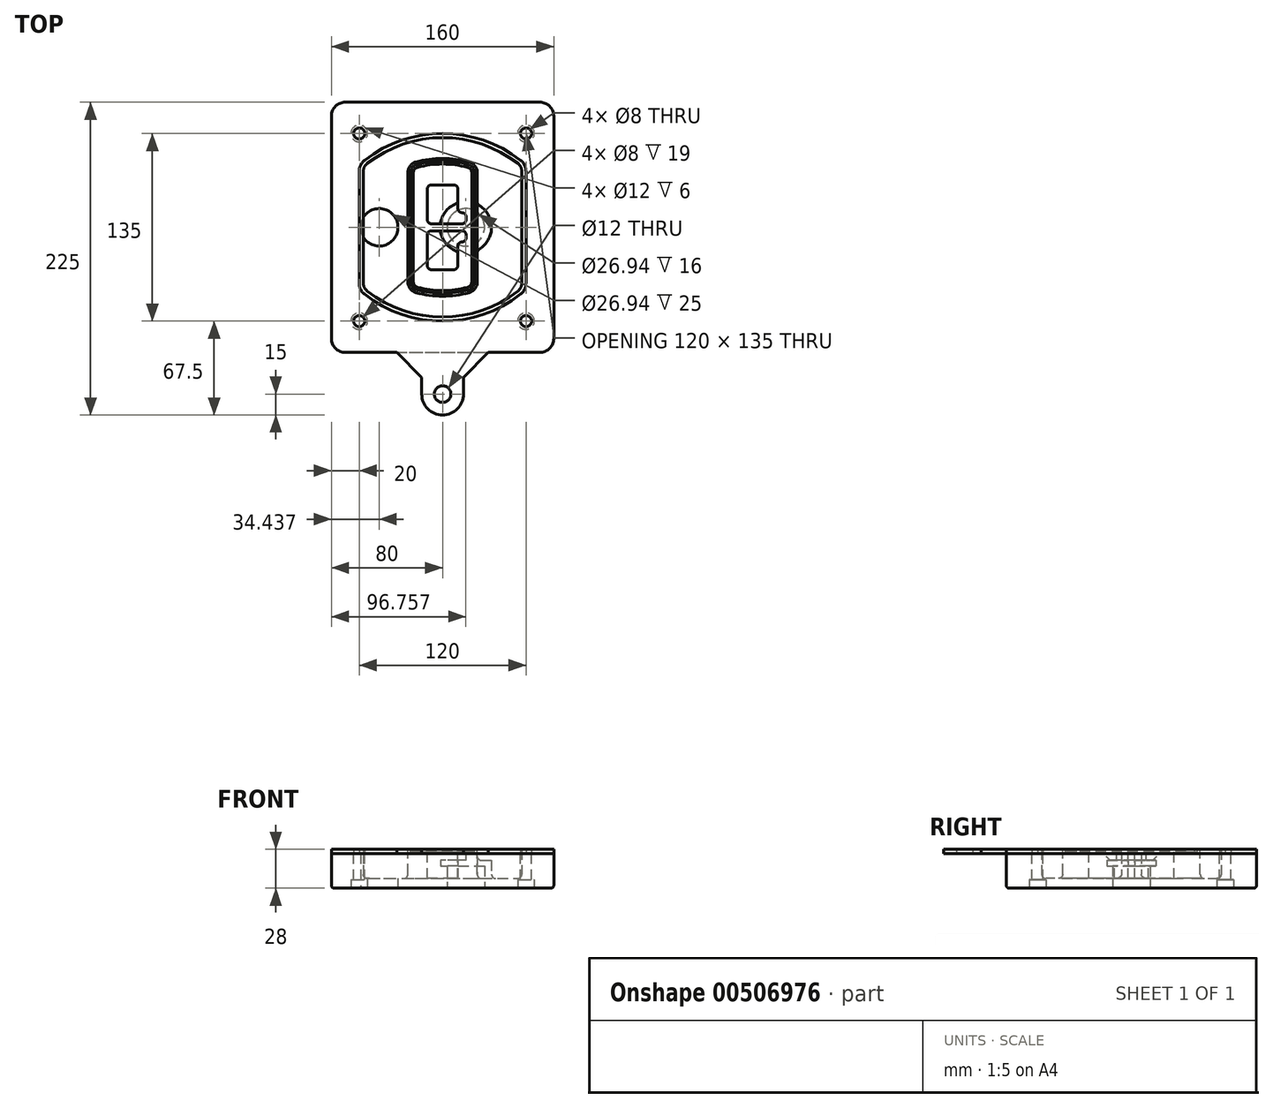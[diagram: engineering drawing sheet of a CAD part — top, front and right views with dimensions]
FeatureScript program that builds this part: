
annotation { "Feature Type Name" : "Feature", "Feature Type Description" : "" }
export const myFeature = defineFeature(function(context is Context, id is Id, definition is map)
    precondition{}
    {
        {
            var Q0;
            Q0=qCreatedBy(makeId("Top.planeOp"),FACE);
            var sketch = newSketch(context, id + "F0", { "sketchPlane" : qUnion([Q0])});
            skPoint(sketch, "E0.rect.middle", {"position": v(0, 0) * mm});
            skLineSegment(sketch, "E1.bottom", {"start": v(-70, -90) * mm, "end": v(70, -90) * mm});
            skLineSegment(sketch, "E1.top", {"start": v(-70, 90) * mm, "end": v(70, 90) * mm});
            skLineSegment(sketch, "E1.left", {"start": v(-80, -80) * mm, "end": v(-80, 80) * mm});
            skLineSegment(sketch, "E1.right", {"start": v(80, -80) * mm, "end": v(80, 80) * mm});
            skLineSegment(sketch, "E2", {"start": v(-80, 90) * mm, "end": v(80, -90) * mm, "construction": true});
            skLineSegment(sketch, "E3", {"start": v(80, 90) * mm, "end": v(-80, -90) * mm, "construction": true});
            skCircle(sketch, "E4", {"center": v(-60, 67.5) * mm, "radius": 4 * mm});
            skCircle(sketch, "E5", {"center": v(60, 67.5) * mm, "radius": 4 * mm});
            skCircle(sketch, "E6", {"center": v(60, -67.5) * mm, "radius": 4 * mm});
            skCircle(sketch, "E7", {"center": v(-60, -67.5) * mm, "radius": 4 * mm});
            skLineSegment(sketch, "E8", {"start": v(-60, 67.5) * mm, "end": v(60, 67.5) * mm, "construction": true});
            skLineSegment(sketch, "E9", {"start": v(60, 67.5) * mm, "end": v(60, -67.5) * mm, "construction": true});
            skLineSegment(sketch, "E10", {"start": v(60, -67.5) * mm, "end": v(-60, -67.5) * mm, "construction": true});
            skLineSegment(sketch, "E11", {"start": v(-60, -67.5) * mm, "end": v(-60, 67.5) * mm, "construction": true});
            skLineSegment(sketch, "E12", {"start": v(-60, 40.3) * mm, "end": v(-60, -40.3) * mm});
            skLineSegment(sketch, "E13", {"start": v(60, 40.3) * mm, "end": v(60, -40.3) * mm});
            skArc(sketch, "E14", {"start": v(56.15, 48.18) * mm, "mid": v(0, 67.5) * mm, "end": v(-56.15, 48.18) * mm});
            skArc(sketch, "E15", {"start": v(-56.15, -48.18) * mm, "mid": v(0, -67.5) * mm, "end": v(56.15, -48.18) * mm});
            skLineSegment(sketch, "E16", {"start": v(-60, 0) * mm, "end": v(60, 0) * mm, "construction": true});
            skPoint(sketch, "E17.visualSharp", {"position": v(-60, -45) * mm});
            skArc(sketch, "E17.filletArc", {"start": v(-60, -40.3) * mm, "mid": v(-58.99, -44.68) * mm, "end": v(-56.15, -48.18) * mm});
            skPoint(sketch, "E18.visualSharp", {"position": v(-60, 45) * mm});
            skArc(sketch, "E18.filletArc", {"start": v(-56.15, 48.18) * mm, "mid": v(-58.99, 44.68) * mm, "end": v(-60, 40.3) * mm});
            skPoint(sketch, "E19.visualSharp", {"position": v(60, 45) * mm});
            skArc(sketch, "E19.filletArc", {"start": v(60, 40.3) * mm, "mid": v(58.99, 44.68) * mm, "end": v(56.15, 48.18) * mm});
            skPoint(sketch, "E20.visualSharp", {"position": v(60, -45) * mm});
            skArc(sketch, "E20.filletArc", {"start": v(56.15, -48.18) * mm, "mid": v(58.99, -44.68) * mm, "end": v(60, -40.3) * mm});
            skPoint(sketch, "E21.visualSharp", {"position": v(-80, 90) * mm});
            skArc(sketch, "E21.filletArc", {"start": v(-70, 90) * mm, "mid": v(-77.07, 87.07) * mm, "end": v(-80, 80) * mm});
            skPoint(sketch, "E22.visualSharp", {"position": v(80, 90) * mm});
            skArc(sketch, "E22.filletArc", {"start": v(80, 80) * mm, "mid": v(77.07, 87.07) * mm, "end": v(70, 90) * mm});
            skPoint(sketch, "E23.visualSharp", {"position": v(80, -90) * mm});
            skArc(sketch, "E23.filletArc", {"start": v(70, -90) * mm, "mid": v(77.07, -87.07) * mm, "end": v(80, -80) * mm});
            skPoint(sketch, "E24.visualSharp", {"position": v(-80, -90) * mm});
            skArc(sketch, "E24.filletArc", {"start": v(-80, -80) * mm, "mid": v(-77.07, -87.07) * mm, "end": v(-70, -90) * mm});
            skArc(sketch, "E25.0", {"start": v(57, 40.3) * mm, "mid": v(56.3, 43.36) * mm, "end": v(54.3, 45.81) * mm});
            skLineSegment(sketch, "E25.1", {"start": v(57, 40.3) * mm, "end": v(57, -40.3) * mm});
            skArc(sketch, "E25.2", {"start": v(54.3, -45.81) * mm, "mid": v(56.3, -43.36) * mm, "end": v(57, -40.3) * mm});
            skArc(sketch, "E25.3", {"start": v(-54.3, -45.81) * mm, "mid": v(0, -64.5) * mm, "end": v(54.3, -45.81) * mm});
            skArc(sketch, "E25.4", {"start": v(-57, -40.3) * mm, "mid": v(-56.3, -43.36) * mm, "end": v(-54.3, -45.81) * mm});
            skArc(sketch, "E25.5", {"start": v(54.3, 45.81) * mm, "mid": v(0, 64.5) * mm, "end": v(-54.3, 45.81) * mm});
            skLineSegment(sketch, "E25.6", {"start": v(-57, 40.3) * mm, "end": v(-57, -40.3) * mm});
            skArc(sketch, "E25.7", {"start": v(-54.3, 45.81) * mm, "mid": v(-56.3, 43.36) * mm, "end": v(-57, 40.3) * mm});
            skArc(sketch, "E26.0", {"start": v(-58.62, 51.33) * mm, "mid": v(-62.58, 46.43) * mm, "end": v(-64, 40.3) * mm});
            skArc(sketch, "E26.1", {"start": v(58.62, 51.33) * mm, "mid": v(0, 71.5) * mm, "end": v(-58.62, 51.33) * mm});
            skArc(sketch, "E26.2", {"start": v(64, 40.3) * mm, "mid": v(62.58, 46.43) * mm, "end": v(58.62, 51.33) * mm});
            skLineSegment(sketch, "E26.3", {"start": v(64, 40.3) * mm, "end": v(64, -40.3) * mm});
            skArc(sketch, "E26.4", {"start": v(58.62, -51.33) * mm, "mid": v(62.58, -46.43) * mm, "end": v(64, -40.3) * mm});
            skLineSegment(sketch, "E26.5", {"start": v(-64, 40.3) * mm, "end": v(-64, -40.3) * mm});
            skArc(sketch, "E26.6", {"start": v(-58.62, -51.33) * mm, "mid": v(0, -71.5) * mm, "end": v(58.62, -51.33) * mm});
            skArc(sketch, "E26.7", {"start": v(-64, -40.3) * mm, "mid": v(-62.58, -46.43) * mm, "end": v(-58.62, -51.33) * mm});
            skSolve(sketch);
        }
        {
            var Q0;
            Q0=makeQuery(id+"F0.imprint","IMPRINT",FACE,{"disambiguationData":[TD([[makeQuery(id+"F0.imprint","IMPRINT",EDGE,{"derivedFrom":sQuery(id+"F0.wireOp",EDGE,"E1.bottom")}),1.0]])]});
            var Q1;
            Q1=makeQuery(id+"F0.imprint","IMPRINT",FACE,{"disambiguationData":[TD([[makeQuery(id+"F0.imprint","IMPRINT",EDGE,{"derivedFrom":sQuery(id+"F0.wireOp",EDGE,"E12")}),1.0]])]});
            var Q2;
            Q2=makeQuery(id+"F0.imprint","IMPRINT",FACE,{"disambiguationData":[TD([[makeQuery(id+"F0.imprint","IMPRINT",EDGE,{"derivedFrom":sQuery(id+"F0.wireOp",EDGE,"E25.0")}),1.0]])]});
            var Q3;
            Q3=makeQuery(id+"F0.imprint","IMPRINT",FACE,{"disambiguationData":[TD([[makeQuery(id+"F0.imprint","IMPRINT",EDGE,{"derivedFrom":sQuery(id+"F0.wireOp",EDGE,"E12")}),-1.0]])]});
            extrude(context, id + "F1", {"entities" : qUnion([Q0, Q1, Q2, Q3]), "oppositeDirection" : true, "depth" : 25 * mm});
        }
        {
            var Q0;
            Q0=makeQuery(id+"F0.imprint","IMPRINT",FACE,{"disambiguationData":[TD([[makeQuery(id+"F0.imprint","IMPRINT",EDGE,{"derivedFrom":sQuery(id+"F0.wireOp",EDGE,"E12")}),1.0]])]});
            extrude(context, id + "F2", {"entities" : qUnion([Q0]), "operationType" : NewBodyOperationType.ADD, "depth" : 3 * mm});
        }
        {
            var Q0;
            Q0=makeQuery(id+"F0.imprint","IMPRINT",FACE,{"disambiguationData":[TD([[makeQuery(id+"F0.imprint","IMPRINT",EDGE,{"derivedFrom":sQuery(id+"F0.wireOp",EDGE,"E25.0")}),1.0]])]});
            extrude(context, id + "F3", {"entities" : qUnion([Q0]), "operationType" : NewBodyOperationType.REMOVE, "oppositeDirection" : true, "depth" : 18 * mm});
        }
        {
            var Q0;
            Q0=makeQuery(id+"F2.opExtrude","CAP_FACE",FACE,{"disambiguationData":[OSD([sQuery(id+"F0.wireOp",EDGE,"E12"),sQuery(id+"F0.wireOp",EDGE,"E13"),sQuery(id+"F0.wireOp",EDGE,"E14"),sQuery(id+"F0.wireOp",EDGE,"E15"),sQuery(id+"F0.wireOp",EDGE,"E17.filletArc"),sQuery(id+"F0.wireOp",EDGE,"E18.filletArc"),sQuery(id+"F0.wireOp",EDGE,"E19.filletArc"),sQuery(id+"F0.wireOp",EDGE,"E20.filletArc"),sQuery(id+"F0.wireOp",EDGE,"E25.0"),sQuery(id+"F0.wireOp",EDGE,"E25.1"),sQuery(id+"F0.wireOp",EDGE,"E25.2"),sQuery(id+"F0.wireOp",EDGE,"E25.3"),sQuery(id+"F0.wireOp",EDGE,"E25.4"),sQuery(id+"F0.wireOp",EDGE,"E25.5"),sQuery(id+"F0.wireOp",EDGE,"E25.6"),sQuery(id+"F0.wireOp",EDGE,"E25.7")])],"isStart":false});
            var sketch = newSketch(context, id + "F4", { "sketchPlane" : qUnion([Q0])});
            skArc(sketch, "E27.0", {"start": v(-19.08, -46.97) * mm, "mid": v(0, -49.5) * mm, "end": v(19.08, -46.97) * mm});
            skArc(sketch, "E28.0", {"start": v(19.08, 46.97) * mm, "mid": v(0, 49.5) * mm, "end": v(-19.08, 46.97) * mm});
            skLineSegment(sketch, "E29", {"start": v(-25, 39.25) * mm, "end": v(-25, -39.25) * mm});
            skLineSegment(sketch, "E30", {"start": v(25, 39.25) * mm, "end": v(25, -39.25) * mm});
            skLineSegment(sketch, "E31", {"start": v(-25, 45.1) * mm, "end": v(25, 45.1) * mm, "construction": true});
            skLineSegment(sketch, "E32", {"start": v(-25, -45.1) * mm, "end": v(25, -45.1) * mm, "construction": true});
            skPoint(sketch, "E33.visualSharp", {"position": v(-25, 45.1) * mm});
            skArc(sketch, "E33.filletArc", {"start": v(-19.08, 46.97) * mm, "mid": v(-23.35, 44.11) * mm, "end": v(-25, 39.25) * mm});
            skPoint(sketch, "E34.visualSharp", {"position": v(25, 45.1) * mm});
            skArc(sketch, "E34.filletArc", {"start": v(25, 39.25) * mm, "mid": v(23.35, 44.11) * mm, "end": v(19.08, 46.97) * mm});
            skPoint(sketch, "E35.visualSharp", {"position": v(25, -45.1) * mm});
            skArc(sketch, "E35.filletArc", {"start": v(19.08, -46.97) * mm, "mid": v(23.35, -44.11) * mm, "end": v(25, -39.25) * mm});
            skPoint(sketch, "E36.visualSharp", {"position": v(-25, -45.1) * mm});
            skArc(sketch, "E36.filletArc", {"start": v(-25, -39.25) * mm, "mid": v(-23.35, -44.11) * mm, "end": v(-19.08, -46.97) * mm});
            skArc(sketch, "E37.0", {"start": v(54.3, 45.81) * mm, "mid": v(0, 64.5) * mm, "end": v(-54.3, 45.81) * mm});
            skArc(sketch, "E37.1", {"start": v(-54.3, 45.81) * mm, "mid": v(-56.3, 43.36) * mm, "end": v(-57, 40.3) * mm});
            skLineSegment(sketch, "E37.2", {"start": v(-57, 40.3) * mm, "end": v(-57, -40.3) * mm});
            skArc(sketch, "E37.3", {"start": v(-57, -40.3) * mm, "mid": v(-56.3, -43.36) * mm, "end": v(-54.3, -45.81) * mm});
            skArc(sketch, "E37.4", {"start": v(-54.3, -45.81) * mm, "mid": v(0, -64.5) * mm, "end": v(54.3, -45.81) * mm});
            skArc(sketch, "E37.5", {"start": v(54.3, -45.81) * mm, "mid": v(56.3, -43.36) * mm, "end": v(57, -40.3) * mm});
            skLineSegment(sketch, "E37.6", {"start": v(57, 40.3) * mm, "end": v(57, -40.3) * mm});
            skArc(sketch, "E37.7", {"start": v(57, 40.3) * mm, "mid": v(56.3, 43.36) * mm, "end": v(54.3, 45.81) * mm});
            skLineSegment(sketch, "E38.0", {"start": v(23, 39.25) * mm, "end": v(23, -39.25) * mm});
            skArc(sketch, "E38.1", {"start": v(18.56, -45.04) * mm, "mid": v(21.76, -42.9) * mm, "end": v(23, -39.25) * mm});
            skArc(sketch, "E38.2", {"start": v(-18.56, -45.04) * mm, "mid": v(0, -47.5) * mm, "end": v(18.56, -45.04) * mm});
            skArc(sketch, "E38.3", {"start": v(-23, -39.25) * mm, "mid": v(-21.76, -42.9) * mm, "end": v(-18.56, -45.04) * mm});
            skLineSegment(sketch, "E38.4", {"start": v(-23, 39.25) * mm, "end": v(-23, -39.25) * mm});
            skArc(sketch, "E38.5", {"start": v(23, 39.25) * mm, "mid": v(21.76, 42.9) * mm, "end": v(18.56, 45.04) * mm});
            skArc(sketch, "E38.6", {"start": v(-18.56, 45.04) * mm, "mid": v(-21.76, 42.9) * mm, "end": v(-23, 39.25) * mm});
            skArc(sketch, "E38.7", {"start": v(18.56, 45.04) * mm, "mid": v(0, 47.5) * mm, "end": v(-18.56, 45.04) * mm});
            skArc(sketch, "E39.0", {"start": v(21, 39.25) * mm, "mid": v(20.18, 41.68) * mm, "end": v(18.04, 43.1) * mm});
            skLineSegment(sketch, "E39.1", {"start": v(21, 39.25) * mm, "end": v(21, -39.25) * mm});
            skArc(sketch, "E39.2", {"start": v(18.04, -43.1) * mm, "mid": v(20.18, -41.68) * mm, "end": v(21, -39.25) * mm});
            skArc(sketch, "E39.3", {"start": v(-18.04, -43.1) * mm, "mid": v(0, -45.5) * mm, "end": v(18.04, -43.1) * mm});
            skArc(sketch, "E39.4", {"start": v(-21, -39.25) * mm, "mid": v(-20.18, -41.68) * mm, "end": v(-18.04, -43.1) * mm});
            skArc(sketch, "E39.5", {"start": v(18.04, 43.1) * mm, "mid": v(0, 45.5) * mm, "end": v(-18.04, 43.1) * mm});
            skLineSegment(sketch, "E39.6", {"start": v(-21, 39.25) * mm, "end": v(-21, -39.25) * mm});
            skArc(sketch, "E39.7", {"start": v(-18.04, 43.1) * mm, "mid": v(-20.18, 41.68) * mm, "end": v(-21, 39.25) * mm});
            skLineSegment(sketch, "E40", {"start": v(-25, 0) * mm, "end": v(25, 0) * mm, "construction": true});
            skLineSegment(sketch, "E41", {"start": v(-11, 5.5) * mm, "end": v(-11, 27.5) * mm});
            skLineSegment(sketch, "E42", {"start": v(-8, 30.5) * mm, "end": v(8, 30.5) * mm});
            skLineSegment(sketch, "E43", {"start": v(11, 27.5) * mm, "end": v(11, 13.5) * mm});
            skLineSegment(sketch, "E44", {"start": v(14, 10.5) * mm, "end": v(14, 10.5) * mm});
            skLineSegment(sketch, "E45", {"start": v(17, 7.5) * mm, "end": v(17, 5.5) * mm});
            skLineSegment(sketch, "E46", {"start": v(14, 2.5) * mm, "end": v(-8, 2.5) * mm});
            skPoint(sketch, "E47.visualSharp", {"position": v(-11, 30.5) * mm});
            skArc(sketch, "E47.filletArc", {"start": v(-8, 30.5) * mm, "mid": v(-10.12, 29.62) * mm, "end": v(-11, 27.5) * mm});
            skPoint(sketch, "E48.visualSharp", {"position": v(11, 30.5) * mm});
            skArc(sketch, "E48.filletArc", {"start": v(11, 27.5) * mm, "mid": v(10.12, 29.62) * mm, "end": v(8, 30.5) * mm});
            skPoint(sketch, "E49.visualSharp", {"position": v(11, 10.5) * mm});
            skArc(sketch, "E49.filletArc", {"start": v(11, 13.5) * mm, "mid": v(11.88, 11.38) * mm, "end": v(14, 10.5) * mm});
            skPoint(sketch, "E50.visualSharp", {"position": v(17, 10.5) * mm});
            skArc(sketch, "E50.filletArc", {"start": v(17, 7.5) * mm, "mid": v(16.12, 9.62) * mm, "end": v(14, 10.5) * mm});
            skPoint(sketch, "E51.visualSharp", {"position": v(17, 2.5) * mm});
            skArc(sketch, "E51.filletArc", {"start": v(14, 2.5) * mm, "mid": v(16.12, 3.38) * mm, "end": v(17, 5.5) * mm});
            skPoint(sketch, "E52.visualSharp", {"position": v(-11, 2.5) * mm});
            skArc(sketch, "E52.filletArc", {"start": v(-11, 5.5) * mm, "mid": v(-10.12, 3.38) * mm, "end": v(-8, 2.5) * mm});
            skLineSegment(sketch, "E53.0.MirrorCS", {"start": v(14, -2.5) * mm, "end": v(-8, -2.5) * mm});
            skArc(sketch, "E54.0.MirrorCS", {"start": v(-11, -5.5) * mm, "mid": v(-10.12, -3.38) * mm, "end": v(-8, -2.5) * mm});
            skLineSegment(sketch, "E55.0.MirrorCS", {"start": v(-11, -5.5) * mm, "end": v(-11, -27.5) * mm});
            skArc(sketch, "E56.0.MirrorCS", {"start": v(-8, -30.5) * mm, "mid": v(-10.12, -29.62) * mm, "end": v(-11, -27.5) * mm});
            skLineSegment(sketch, "E57.0.MirrorCS", {"start": v(-8, -30.5) * mm, "end": v(8, -30.5) * mm});
            skArc(sketch, "E58.0.MirrorCS", {"start": v(11, -27.5) * mm, "mid": v(10.12, -29.62) * mm, "end": v(8, -30.5) * mm});
            skLineSegment(sketch, "E59.0.MirrorCS", {"start": v(11, -27.5) * mm, "end": v(11, -13.5) * mm});
            skArc(sketch, "E60.0.MirrorCS", {"start": v(11, -13.5) * mm, "mid": v(11.88, -11.38) * mm, "end": v(14, -10.5) * mm});
            skArc(sketch, "E61.0.MirrorCS", {"start": v(17, -7.5) * mm, "mid": v(16.12, -9.62) * mm, "end": v(14, -10.5) * mm});
            skLineSegment(sketch, "E62.0.MirrorCS", {"start": v(17, -7.5) * mm, "end": v(17, -5.5) * mm});
            skArc(sketch, "E63.0.MirrorCS", {"start": v(14, -2.5) * mm, "mid": v(16.12, -3.38) * mm, "end": v(17, -5.5) * mm});
            skSolve(sketch);
        }
        {
            var Q0;
            Q0=makeQuery(id+"F4.imprint","IMPRINT",FACE,{"disambiguationData":[TD([[makeQuery(id+"F4.imprint","IMPRINT",EDGE,{"derivedFrom":sQuery(id+"F4.wireOp",EDGE,"E27.0")}),1.0]])]});
            var Q1;
            Q1=makeQuery(id+"F4.imprint","IMPRINT",FACE,{"disambiguationData":[TD([[makeQuery(id+"F4.imprint","IMPRINT",EDGE,{"derivedFrom":sQuery(id+"F4.wireOp",EDGE,"E38.0")}),-1.0]])]});
            var Q2;
            Q2=makeQuery(id+"F4.imprint","IMPRINT",FACE,{"disambiguationData":[TD([[makeQuery(id+"F4.imprint","IMPRINT",EDGE,{"derivedFrom":sQuery(id+"F4.wireOp",EDGE,"E39.0")}),1.0]])]});
            extrude(context, id + "F5", {"entities" : qUnion([Q0, Q1, Q2]), "operationType" : NewBodyOperationType.ADD, "endBound" : BoundingType.UP_TO_NEXT, "oppositeDirection" : true, "depth" : 25 * mm});
        }
        {
            var Q0;
            Q0=makeQuery(id+"F4.imprint","IMPRINT",FACE,{"disambiguationData":[TD([[makeQuery(id+"F4.imprint","IMPRINT",EDGE,{"derivedFrom":sQuery(id+"F4.wireOp",EDGE,"E38.0")}),-1.0]])]});
            extrude(context, id + "F6", {"entities" : qUnion([Q0]), "operationType" : NewBodyOperationType.REMOVE, "oppositeDirection" : true, "depth" : 2 * mm});
        }
        {
            var Q0;
            Q0=makeQuery(id+"F1.opExtrude","CAP_FACE",FACE,{"disambiguationData":[OSD([sQuery(id+"F0.wireOp",EDGE,"E1.bottom"),sQuery(id+"F0.wireOp",EDGE,"E1.top"),sQuery(id+"F0.wireOp",EDGE,"E1.left"),sQuery(id+"F0.wireOp",EDGE,"E1.right"),sQuery(id+"F0.wireOp",EDGE,"E4"),sQuery(id+"F0.wireOp",EDGE,"E5"),sQuery(id+"F0.wireOp",EDGE,"E6"),sQuery(id+"F0.wireOp",EDGE,"E7"),sQuery(id+"F0.wireOp",EDGE,"E21.filletArc"),sQuery(id+"F0.wireOp",EDGE,"E22.filletArc"),sQuery(id+"F0.wireOp",EDGE,"E23.filletArc"),sQuery(id+"F0.wireOp",EDGE,"E24.filletArc")])],"isStart":false});
            var sketch = newSketch(context, id + "F7", { "sketchPlane" : qUnion([Q0])});
            skCircle(sketch, "E64", {"center": v(16.76, 0) * mm, "radius": 13.47 * mm});
            skCircle(sketch, "E65", {"center": v(-45.56, 0) * mm, "radius": 13.47 * mm});
            skLineSegment(sketch, "E66", {"start": v(80, 0) * mm, "end": v(-80, 0) * mm});
            skCircle(sketch, "E67", {"center": v(16.76, 0) * mm, "radius": 18.47 * mm});
            skCircle(sketch, "E68", {"center": v(60, -67.5) * mm, "radius": 6 * mm});
            skCircle(sketch, "E69", {"center": v(-60, -67.5) * mm, "radius": 6 * mm});
            skCircle(sketch, "E70", {"center": v(-60, 67.5) * mm, "radius": 6 * mm});
            skCircle(sketch, "E71", {"center": v(60, 67.5) * mm, "radius": 6 * mm});
            skSolve(sketch);
        }
        {
            var Q0;
            {var subQ1=sQuery(id+"F7.wireOp",EDGE,"E66");var subQ4=sQuery(id+"F7.wireOp",EDGE,"E64");var subQ6=makeQuery(id+"F7.imprint","INTERSECT",VERTEX,{"disambiguationData":[OD(0.0)],"derivedFrom":[subQ4,subQ1]});Q0=makeQuery(id+"F7.imprint","IMPRINT",FACE,{"disambiguationData":[TD([[makeQuery(id+"F7.imprint","IMPRINT",EDGE,{"disambiguationData":[TD([[subQ6,-1.0]])],"derivedFrom":subQ4}),-1.0]])]});}
            var Q1;
            {var subQ0=sQuery(id+"F7.wireOp",EDGE,"E66");var subQ1=sQuery(id+"F7.wireOp",EDGE,"E64");var subQ3=makeQuery(id+"F7.imprint","INTERSECT",VERTEX,{"disambiguationData":[OD(0.0)],"derivedFrom":[subQ1,subQ0]});Q1=makeQuery(id+"F7.imprint","IMPRINT",FACE,{"disambiguationData":[TD([[makeQuery(id+"F7.imprint","IMPRINT",EDGE,{"disambiguationData":[TD([[subQ3,-1.0]])],"derivedFrom":subQ1}),1.0]])]});}
            var Q2;
            {var subQ0=sQuery(id+"F7.wireOp",EDGE,"E66");var subQ1=sQuery(id+"F7.wireOp",EDGE,"E64");var subQ3=makeQuery(id+"F7.imprint","INTERSECT",VERTEX,{"disambiguationData":[OD(0.0)],"derivedFrom":[subQ1,subQ0]});Q2=makeQuery(id+"F7.imprint","IMPRINT",FACE,{"disambiguationData":[TD([[makeQuery(id+"F7.imprint","IMPRINT",EDGE,{"disambiguationData":[TD([[subQ3,1.0]])],"derivedFrom":subQ1}),1.0]])]});}
            var Q3;
            {var subQ1=sQuery(id+"F7.wireOp",EDGE,"E66");var subQ4=sQuery(id+"F7.wireOp",EDGE,"E64");var subQ6=makeQuery(id+"F7.imprint","INTERSECT",VERTEX,{"disambiguationData":[OD(0.0)],"derivedFrom":[subQ4,subQ1]});Q3=makeQuery(id+"F7.imprint","IMPRINT",FACE,{"disambiguationData":[TD([[makeQuery(id+"F7.imprint","IMPRINT",EDGE,{"disambiguationData":[TD([[subQ6,1.0]])],"derivedFrom":subQ4}),-1.0]])]});}
            extrude(context, id + "F8", {"entities" : qUnion([Q0, Q1, Q2, Q3]), "operationType" : NewBodyOperationType.ADD, "oppositeDirection" : true, "depth" : 20 * mm});
        }
        {
            var Q0;
            {var subQ0=sQuery(id+"F7.wireOp",EDGE,"E66");var subQ1=sQuery(id+"F7.wireOp",EDGE,"E64");var subQ3=makeQuery(id+"F7.imprint","INTERSECT",VERTEX,{"disambiguationData":[OD(0.0)],"derivedFrom":[subQ1,subQ0]});Q0=makeQuery(id+"F7.imprint","IMPRINT",FACE,{"disambiguationData":[TD([[makeQuery(id+"F7.imprint","IMPRINT",EDGE,{"disambiguationData":[TD([[subQ3,-1.0]])],"derivedFrom":subQ1}),1.0]])]});}
            var Q1;
            {var subQ0=sQuery(id+"F7.wireOp",EDGE,"E66");var subQ1=sQuery(id+"F7.wireOp",EDGE,"E64");var subQ3=makeQuery(id+"F7.imprint","INTERSECT",VERTEX,{"disambiguationData":[OD(0.0)],"derivedFrom":[subQ1,subQ0]});Q1=makeQuery(id+"F7.imprint","IMPRINT",FACE,{"disambiguationData":[TD([[makeQuery(id+"F7.imprint","IMPRINT",EDGE,{"disambiguationData":[TD([[subQ3,1.0]])],"derivedFrom":subQ1}),1.0]])]});}
            extrude(context, id + "F9", {"entities" : qUnion([Q0, Q1]), "operationType" : NewBodyOperationType.REMOVE, "oppositeDirection" : true, "depth" : 16 * mm});
        }
        {
            var Q0;
            {var subQ0=sQuery(id+"F7.wireOp",EDGE,"E66");var subQ1=sQuery(id+"F7.wireOp",EDGE,"E65");var subQ3=makeQuery(id+"F7.imprint","INTERSECT",VERTEX,{"disambiguationData":[OD(0.0)],"derivedFrom":[subQ1,subQ0]});Q0=makeQuery(id+"F7.imprint","IMPRINT",FACE,{"disambiguationData":[TD([[makeQuery(id+"F7.imprint","IMPRINT",EDGE,{"disambiguationData":[TD([[subQ3,-1.0]])],"derivedFrom":subQ1}),1.0]])]});}
            var Q1;
            {var subQ0=sQuery(id+"F7.wireOp",EDGE,"E66");var subQ1=sQuery(id+"F7.wireOp",EDGE,"E65");var subQ3=makeQuery(id+"F7.imprint","INTERSECT",VERTEX,{"disambiguationData":[OD(0.0)],"derivedFrom":[subQ1,subQ0]});Q1=makeQuery(id+"F7.imprint","IMPRINT",FACE,{"disambiguationData":[TD([[makeQuery(id+"F7.imprint","IMPRINT",EDGE,{"disambiguationData":[TD([[subQ3,1.0]])],"derivedFrom":subQ1}),1.0]])]});}
            extrude(context, id + "F10", {"entities" : qUnion([Q0, Q1]), "operationType" : NewBodyOperationType.REMOVE, "oppositeDirection" : true, "depth" : 25 * mm});
        }
        {
            var Q0;
            Q0=makeQuery(id+"F7.imprint","IMPRINT",FACE,{"disambiguationData":[TD([[makeQuery(id+"F7.imprint","IMPRINT",EDGE,{"derivedFrom":sQuery(id+"F7.wireOp",EDGE,"E68")}),1.0]])]});
            var Q1;
            Q1=makeQuery(id+"F7.imprint","IMPRINT",FACE,{"disambiguationData":[TD([[makeQuery(id+"F7.imprint","IMPRINT",EDGE,{"derivedFrom":makeQuery(id+"F1.opExtrude","CAP_EDGE",EDGE,{"disambiguationData":[OSD([sQuery(id+"F0.wireOp",EDGE,"E5")])],"isStart":false})}),-1.0]])]});
            var Q2;
            Q2=makeQuery(id+"F7.imprint","IMPRINT",FACE,{"disambiguationData":[TD([[makeQuery(id+"F7.imprint","IMPRINT",EDGE,{"derivedFrom":sQuery(id+"F7.wireOp",EDGE,"E69")}),1.0]])]});
            var Q3;
            Q3=makeQuery(id+"F7.imprint","IMPRINT",FACE,{"disambiguationData":[TD([[makeQuery(id+"F7.imprint","IMPRINT",EDGE,{"derivedFrom":makeQuery(id+"F1.opExtrude","CAP_EDGE",EDGE,{"disambiguationData":[OSD([sQuery(id+"F0.wireOp",EDGE,"E4")])],"isStart":false})}),-1.0]])]});
            var Q4;
            Q4=makeQuery(id+"F7.imprint","IMPRINT",FACE,{"disambiguationData":[TD([[makeQuery(id+"F7.imprint","IMPRINT",EDGE,{"derivedFrom":sQuery(id+"F7.wireOp",EDGE,"E70")}),1.0]])]});
            var Q5;
            Q5=makeQuery(id+"F7.imprint","IMPRINT",FACE,{"disambiguationData":[TD([[makeQuery(id+"F7.imprint","IMPRINT",EDGE,{"derivedFrom":makeQuery(id+"F1.opExtrude","CAP_EDGE",EDGE,{"disambiguationData":[OSD([sQuery(id+"F0.wireOp",EDGE,"E7")])],"isStart":false})}),-1.0]])]});
            var Q6;
            Q6=makeQuery(id+"F7.imprint","IMPRINT",FACE,{"disambiguationData":[TD([[makeQuery(id+"F7.imprint","IMPRINT",EDGE,{"derivedFrom":sQuery(id+"F7.wireOp",EDGE,"E71")}),1.0]])]});
            var Q7;
            Q7=makeQuery(id+"F7.imprint","IMPRINT",FACE,{"disambiguationData":[TD([[makeQuery(id+"F7.imprint","IMPRINT",EDGE,{"derivedFrom":makeQuery(id+"F1.opExtrude","CAP_EDGE",EDGE,{"disambiguationData":[OSD([sQuery(id+"F0.wireOp",EDGE,"E6")])],"isStart":false})}),-1.0]])]});
            extrude(context, id + "F11", {"entities" : qUnion([Q0, Q1, Q2, Q3, Q4, Q5, Q6, Q7]), "operationType" : NewBodyOperationType.REMOVE, "oppositeDirection" : true, "depth" : 6 * mm});
        }
        {
            var Q0;
            Q0=makeQuery(id+"F9.boolean.opBoolean","COPY",FACE,{"derivedFrom":makeQuery(id+"F9.opExtrude","CAP_FACE",FACE,{"disambiguationData":[OSD([sQuery(id+"F7.wireOp",EDGE,"E64")])],"isStart":false})});
            var sketch = newSketch(context, id + "F12", { "sketchPlane" : qUnion([Q0])});
            skArc(sketch, "E72.0", {"start": v(11, 17.55) * mm, "mid": v(2.57, 11.82) * mm, "end": v(-1.54, 2.5) * mm});
            skArc(sketch, "E72.1", {"start": v(-1.54, -2.5) * mm, "mid": v(2.57, -11.82) * mm, "end": v(11, -17.55) * mm});
            skLineSegment(sketch, "E73", {"start": v(-1.54, -2.5) * mm, "end": v(14, -2.5) * mm});
            skLineSegment(sketch, "E74.0", {"start": v(14, 2.5) * mm, "end": v(-1.54, 2.5) * mm});
            skArc(sketch, "E74.1", {"start": v(14, 2.5) * mm, "mid": v(16.12, 3.38) * mm, "end": v(17, 5.5) * mm});
            skLineSegment(sketch, "E74.2", {"start": v(17, 7.5) * mm, "end": v(17, 5.5) * mm});
            skArc(sketch, "E74.3", {"start": v(17, 7.5) * mm, "mid": v(16.12, 9.62) * mm, "end": v(14, 10.5) * mm});
            skArc(sketch, "E74.4", {"start": v(11, 13.5) * mm, "mid": v(11.88, 11.38) * mm, "end": v(14, 10.5) * mm});
            skLineSegment(sketch, "E74.5", {"start": v(11, 17.55) * mm, "end": v(11, 13.5) * mm});
            skLineSegment(sketch, "E74.7", {"start": v(14, -2.5) * mm, "end": v(-1.54, -2.5) * mm});
            skArc(sketch, "E74.8", {"start": v(14, -2.5) * mm, "mid": v(16.12, -3.38) * mm, "end": v(17, -5.5) * mm});
            skLineSegment(sketch, "E74.9", {"start": v(17, -7.5) * mm, "end": v(17, -5.5) * mm});
            skArc(sketch, "E74.10", {"start": v(17, -7.5) * mm, "mid": v(16.12, -9.62) * mm, "end": v(14, -10.5) * mm});
            skArc(sketch, "E74.11", {"start": v(11, -13.5) * mm, "mid": v(11.88, -11.38) * mm, "end": v(14, -10.5) * mm});
            skLineSegment(sketch, "E74.12", {"start": v(11, -17.55) * mm, "end": v(11, -13.5) * mm});
            skPoint(sketch, "E75.orphan", {"position": v(11, -27.5) * mm});
            skPoint(sketch, "E76.orphan", {"position": v(-8, -2.5) * mm});
            skPoint(sketch, "E77.orphan", {"position": v(-8, 2.5) * mm});
            skPoint(sketch, "E78.orphan", {"position": v(11, 27.5) * mm});
            skSolve(sketch);
        }
        {
            var Q0;
            {var subQ7=sQuery(id+"F12.wireOp",EDGE,"E72.0");var subQ14=sQuery(id+"F12.wireOp",EDGE,"E72.1");var subQ16=sQuery(id+"F12.wireOp",EDGE,"E74.1");var subQ18=sQuery(id+"F12.wireOp",EDGE,"E74.8");Q0=qUnion([makeQuery(id+"F12.imprint","IMPRINT",FACE,{"disambiguationData":[TD([[makeQuery(id+"F12.imprint","IMPRINT",EDGE,{"derivedFrom":subQ7}),1.0]])]}),makeQuery(id+"F12.imprint","IMPRINT",FACE,{"disambiguationData":[TD([[makeQuery(id+"F12.imprint","IMPRINT",EDGE,{"derivedFrom":subQ14}),1.0]])]}),makeQuery(id+"F12.imprint","IMPRINT",FACE,{"disambiguationData":[TD([[makeQuery(id+"F12.imprint","IMPRINT",EDGE,{"derivedFrom":subQ16}),1.0]])]}),makeQuery(id+"F12.imprint","IMPRINT",FACE,{"disambiguationData":[TD([[makeQuery(id+"F12.imprint","IMPRINT",EDGE,{"derivedFrom":subQ18}),-1.0]])]})]);}
            var Q1;
            Q1=makeQuery(id+"F5.boolean.opBoolean","SPLIT",FACE,{"disambiguationData":[TD([makeQuery(id+"F5.opExtrude","SWEPT_FACE",FACE,{"disambiguationData":[OSD([sQuery(id+"F4.wireOp",EDGE,"E41")])]})])],"derivedFrom":makeQuery(id+"F3.boolean.opBoolean","COPY",FACE,{"derivedFrom":makeQuery(id+"F3.opExtrude","CAP_FACE",FACE,{"disambiguationData":[OSD([sQuery(id+"F0.wireOp",EDGE,"E25.0"),sQuery(id+"F0.wireOp",EDGE,"E25.1"),sQuery(id+"F0.wireOp",EDGE,"E25.2"),sQuery(id+"F0.wireOp",EDGE,"E25.3"),sQuery(id+"F0.wireOp",EDGE,"E25.4"),sQuery(id+"F0.wireOp",EDGE,"E25.5"),sQuery(id+"F0.wireOp",EDGE,"E25.6"),sQuery(id+"F0.wireOp",EDGE,"E25.7")])],"isStart":false})})});
            extrude(context, id + "F13", {"entities" : qUnion([Q0]), "operationType" : NewBodyOperationType.REMOVE, "endBound" : BoundingType.UP_TO_SURFACE, "endBoundEntityFace" : qUnion([Q1]), "depth" : 25 * mm});
        }
        {
            var Q0;
            Q0=makeQuery(id+"F3.boolean.opBoolean","COPY",EDGE,{"derivedFrom":makeQuery(id+"F3.opExtrude","CAP_EDGE",EDGE,{"disambiguationData":[OSD([sQuery(id+"F0.wireOp",EDGE,"E25.6")])],"isStart":false})});
            var Q1;
            Q1=makeQuery(id+"F8.boolean.opBoolean","INTERSECT",EDGE,{"derivedFrom":[makeQuery(id+"F5.opExtrude","SWEPT_FACE",FACE,{"disambiguationData":[OSD([sQuery(id+"F4.wireOp",EDGE,"E30")])]}),makeQuery(id+"F8.opExtrude","CAP_FACE",FACE,{"disambiguationData":[OSD([sQuery(id+"F7.wireOp",EDGE,"E67")])],"isStart":false})]});
            var Q2;
            Q2=makeQuery(id+"F8.boolean.opBoolean","INTERSECT",EDGE,{"disambiguationData":[OD(1.0)],"derivedFrom":[makeQuery(id+"F5.opExtrude","SWEPT_FACE",FACE,{"disambiguationData":[OSD([sQuery(id+"F4.wireOp",EDGE,"E30")])]}),makeQuery(id+"F8.opExtrude","SWEPT_FACE",FACE,{"disambiguationData":[OSD([sQuery(id+"F7.wireOp",EDGE,"E67")])]})]});
            var Q3;
            {var subQ0=sQuery(id+"F4.wireOp",EDGE,"E30");Q3=makeQuery(id+"F8.boolean.opBoolean","SPLIT",EDGE,{"disambiguationData":[TD([makeQuery(id+"F5.opExtrude","SWEPT_FACE",FACE,{"disambiguationData":[OSD([sQuery(id+"F4.wireOp",EDGE,"E35.filletArc")])]})])],"derivedFrom":makeQuery(id+"F5.opExtrude","CAP_EDGE",EDGE,{"disambiguationData":[OSD([subQ0])],"isStart":false})});}
            var Q4;
            {var subQ0=sQuery(id+"F0.wireOp",EDGE,"E25.7");var subQ1=sQuery(id+"F0.wireOp",EDGE,"E25.1");var subQ2=sQuery(id+"F0.wireOp",EDGE,"E25.6");var subQ3=sQuery(id+"F0.wireOp",EDGE,"E25.5");var subQ4=sQuery(id+"F0.wireOp",EDGE,"E25.4");var subQ5=sQuery(id+"F0.wireOp",EDGE,"E25.0");var subQ6=sQuery(id+"F0.wireOp",EDGE,"E25.2");var subQ7=sQuery(id+"F0.wireOp",EDGE,"E25.3");Q4=makeQuery(id+"F8.boolean.opBoolean","INTERSECT",EDGE,{"derivedFrom":[makeQuery(id+"F5.boolean.opBoolean","SPLIT",FACE,{"disambiguationData":[TD([makeQuery(id+"F2.opExtrude","SWEPT_FACE",FACE,{"disambiguationData":[OSD([subQ5])]})])],"derivedFrom":makeQuery(id+"F3.boolean.opBoolean","COPY",FACE,{"derivedFrom":makeQuery(id+"F3.opExtrude","CAP_FACE",FACE,{"disambiguationData":[OSD([subQ5,subQ1,subQ6,subQ7,subQ4,subQ3,subQ2,subQ0])],"isStart":false})})}),makeQuery(id+"F8.opExtrude","SWEPT_FACE",FACE,{"disambiguationData":[OSD([sQuery(id+"F7.wireOp",EDGE,"E67")])]})]});}
            var Q5;
            Q5=makeQuery(id+"F8.boolean.opBoolean","INTERSECT",EDGE,{"disambiguationData":[OD(0.0)],"derivedFrom":[makeQuery(id+"F5.opExtrude","SWEPT_FACE",FACE,{"disambiguationData":[OSD([sQuery(id+"F4.wireOp",EDGE,"E30")])]}),makeQuery(id+"F8.opExtrude","SWEPT_FACE",FACE,{"disambiguationData":[OSD([sQuery(id+"F7.wireOp",EDGE,"E67")])]})]});
            fillet(context, id + "F14", {"entities" : qUnion([Q0, Q1, Q2, Q3, Q4, Q5]), "radius" : 3 * mm, "tangentPropagation" : true, "allowEdgeOverflow" : false});
        }
        {
            var Q0;
            Q0=makeQuery(id+"F1.opExtrude","CAP_EDGE",EDGE,{"disambiguationData":[OSD([sQuery(id+"F0.wireOp",EDGE,"E1.bottom")])],"isStart":false});
            fillet(context, id + "F15", {"entities" : qUnion([Q0]), "radius" : 2 * mm, "tangentPropagation" : true, "allowEdgeOverflow" : false});
        }
        {
            var Q0;
            {var subQ0=sQuery(id+"F0.wireOp",EDGE,"E21.filletArc");var subQ1=sQuery(id+"F0.wireOp",EDGE,"E7");var subQ2=sQuery(id+"F0.wireOp",EDGE,"E6");var subQ3=sQuery(id+"F0.wireOp",EDGE,"E5");var subQ4=sQuery(id+"F0.wireOp",EDGE,"E4");var subQ5=sQuery(id+"F0.wireOp",EDGE,"E22.filletArc");var subQ6=sQuery(id+"F0.wireOp",EDGE,"E1.bottom");var subQ7=sQuery(id+"F0.wireOp",EDGE,"E1.right");var subQ8=sQuery(id+"F0.wireOp",EDGE,"E1.top");var subQ9=sQuery(id+"F0.wireOp",EDGE,"E1.left");var subQ10=sQuery(id+"F0.wireOp",EDGE,"E23.filletArc");var subQ11=sQuery(id+"F0.wireOp",EDGE,"E24.filletArc");Q0=makeQuery(id+"F2.boolean.opBoolean","SPLIT",FACE,{"disambiguationData":[TD([makeQuery(id+"F1.opExtrude","SWEPT_FACE",FACE,{"disambiguationData":[OSD([subQ6])]})])],"derivedFrom":makeQuery(id+"F1.opExtrude","CAP_FACE",FACE,{"disambiguationData":[OSD([subQ6,subQ8,subQ9,subQ7,subQ4,subQ3,subQ2,subQ1,subQ0,subQ5,subQ10,subQ11])],"isStart":true})});}
            var sketch = newSketch(context, id + "F16", { "sketchPlane" : qUnion([Q0])});
            skLineSegment(sketch, "E79.0", {"start": v(-70, 90) * mm, "end": v(70, 90) * mm});
            skArc(sketch, "E79.1", {"start": v(80, 80) * mm, "mid": v(77.07, 87.07) * mm, "end": v(70, 90) * mm});
            skLineSegment(sketch, "E79.2", {"start": v(80, -80) * mm, "end": v(80, 80) * mm});
            skArc(sketch, "E79.3", {"start": v(70, -90) * mm, "mid": v(77.07, -87.07) * mm, "end": v(80, -80) * mm});
            skLineSegment(sketch, "E79.4", {"start": v(-70, -90) * mm, "end": v(70, -90) * mm});
            skArc(sketch, "E79.5", {"start": v(-80, -80) * mm, "mid": v(-77.07, -87.07) * mm, "end": v(-70, -90) * mm});
            skLineSegment(sketch, "E79.6", {"start": v(-80, -80) * mm, "end": v(-80, 80) * mm});
            skArc(sketch, "E79.7", {"start": v(-70, 90) * mm, "mid": v(-77.07, 87.07) * mm, "end": v(-80, 80) * mm});
            skCircle(sketch, "E79.8", {"center": v(60, 67.5) * mm, "radius": 4 * mm});
            skCircle(sketch, "E79.9", {"center": v(60, -67.5) * mm, "radius": 4 * mm});
            skCircle(sketch, "E79.10", {"center": v(-60, -67.5) * mm, "radius": 4 * mm});
            skCircle(sketch, "E79.11", {"center": v(-60, 67.5) * mm, "radius": 4 * mm});
            skArc(sketch, "E79.12", {"start": v(56.15, 48.18) * mm, "mid": v(0, 67.5) * mm, "end": v(-56.15, 48.18) * mm});
            skArc(sketch, "E79.13", {"start": v(60, 40.3) * mm, "mid": v(58.99, 44.68) * mm, "end": v(56.15, 48.18) * mm});
            skLineSegment(sketch, "E79.14", {"start": v(60, 40.3) * mm, "end": v(60, -40.3) * mm});
            skArc(sketch, "E79.15", {"start": v(56.15, -48.18) * mm, "mid": v(58.99, -44.68) * mm, "end": v(60, -40.3) * mm});
            skArc(sketch, "E79.16", {"start": v(-56.15, -48.18) * mm, "mid": v(0, -67.5) * mm, "end": v(56.15, -48.18) * mm});
            skArc(sketch, "E79.17", {"start": v(-60, -40.3) * mm, "mid": v(-58.99, -44.68) * mm, "end": v(-56.15, -48.18) * mm});
            skLineSegment(sketch, "E79.18", {"start": v(-60, 40.3) * mm, "end": v(-60, -40.3) * mm});
            skArc(sketch, "E79.19", {"start": v(-56.15, 48.18) * mm, "mid": v(-58.99, 44.68) * mm, "end": v(-60, 40.3) * mm});
            skLineSegment(sketch, "E80", {"start": v(0, 90) * mm, "end": v(0, 120) * mm, "construction": true});
            skPoint(sketch, "E80.endSnap0", {"position": v(0, 90) * mm});
            skCircle(sketch, "E81", {"center": v(0, 120) * mm, "radius": 6 * mm});
            skLineSegment(sketch, "E82", {"start": v(-15, 108) * mm, "end": v(-33, 90) * mm});
            skLineSegment(sketch, "E83", {"start": v(15, 108) * mm, "end": v(33, 90) * mm});
            skLineSegment(sketch, "E84", {"start": v(-15, 108) * mm, "end": v(-15, 120) * mm});
            skLineSegment(sketch, "E85", {"start": v(15, 108) * mm, "end": v(15, 120) * mm});
            skArc(sketch, "E86", {"start": v(-15, 120) * mm, "mid": v(0, 135) * mm, "end": v(15, 120) * mm});
            skLineSegment(sketch, "E87", {"start": v(-80, 0) * mm, "end": v(80, 0) * mm, "construction": true});
            skLineSegment(sketch, "E88.MirrorCS", {"start": v(80, 0) * mm, "end": v(-80, 0) * mm, "construction": true});
            skArc(sketch, "E89.MirrorCS", {"start": v(15, 120) * mm, "mid": v(0, 135) * mm, "end": v(-15, 120) * mm});
            skLineSegment(sketch, "E90.MirrorCS", {"start": v(0, -90) * mm, "end": v(0, -120) * mm, "construction": true});
            skLineSegment(sketch, "E91.MirrorCS", {"start": v(15, -108) * mm, "end": v(33, -90) * mm});
            skLineSegment(sketch, "E92.MirrorCS", {"start": v(15, -108) * mm, "end": v(15, -120) * mm});
            skArc(sketch, "E93.MirrorCS", {"start": v(-15, -120) * mm, "mid": v(0, -135) * mm, "end": v(15, -120) * mm});
            skCircle(sketch, "E94.MirrorC", {"center": v(0, -120) * mm, "radius": 6 * mm});
            skLineSegment(sketch, "E95.MirrorCS", {"start": v(-15, -108) * mm, "end": v(-33, -90) * mm});
            skLineSegment(sketch, "E96.MirrorCS", {"start": v(-15, -108) * mm, "end": v(-15, -120) * mm});
            skSolve(sketch);
        }
        {
            var Q0;
            {var subQ0=sQuery(id+"F16.wireOp",EDGE,"E91.MirrorCS");Q0=makeQuery(id+"F16.imprint","IMPRINT",FACE,{"disambiguationData":[TD([[makeQuery(id+"F16.imprint","IMPRINT",EDGE,{"derivedFrom":subQ0}),1.0]])]});}
            var Q1;
            {var subQ1=sQuery(id+"F16.wireOp",EDGE,"E79.1");Q1=makeQuery(id+"F16.imprint","IMPRINT",FACE,{"disambiguationData":[TD([[makeQuery(id+"F16.imprint","IMPRINT",EDGE,{"derivedFrom":subQ1}),1.0]])]});}
            var Q2;
            Q2=makeQuery(id+"F16.imprint","IMPRINT",FACE,{"disambiguationData":[TD([[makeQuery(id+"F16.imprint","IMPRINT",EDGE,{"derivedFrom":sQuery(id+"F16.wireOp",EDGE,"E89.MirrorCS")}),1.0]])]});
            var Q3;
            Q3=makeQuery(id+"F2.opExtrude","CAP_FACE",FACE,{"disambiguationData":[OSD([sQuery(id+"F0.wireOp",EDGE,"E12"),sQuery(id+"F0.wireOp",EDGE,"E13"),sQuery(id+"F0.wireOp",EDGE,"E14"),sQuery(id+"F0.wireOp",EDGE,"E15"),sQuery(id+"F0.wireOp",EDGE,"E17.filletArc"),sQuery(id+"F0.wireOp",EDGE,"E18.filletArc"),sQuery(id+"F0.wireOp",EDGE,"E19.filletArc"),sQuery(id+"F0.wireOp",EDGE,"E20.filletArc"),sQuery(id+"F0.wireOp",EDGE,"E25.0"),sQuery(id+"F0.wireOp",EDGE,"E25.1"),sQuery(id+"F0.wireOp",EDGE,"E25.2"),sQuery(id+"F0.wireOp",EDGE,"E25.3"),sQuery(id+"F0.wireOp",EDGE,"E25.4"),sQuery(id+"F0.wireOp",EDGE,"E25.5"),sQuery(id+"F0.wireOp",EDGE,"E25.6"),sQuery(id+"F0.wireOp",EDGE,"E25.7")])],"isStart":false});
            extrude(context, id + "F17", {"entities" : qUnion([Q0, Q1, Q2]), "endBound" : BoundingType.UP_TO_SURFACE, "endBoundEntityFace" : qUnion([Q3]), "depth" : 25 * mm});
        }
    });
